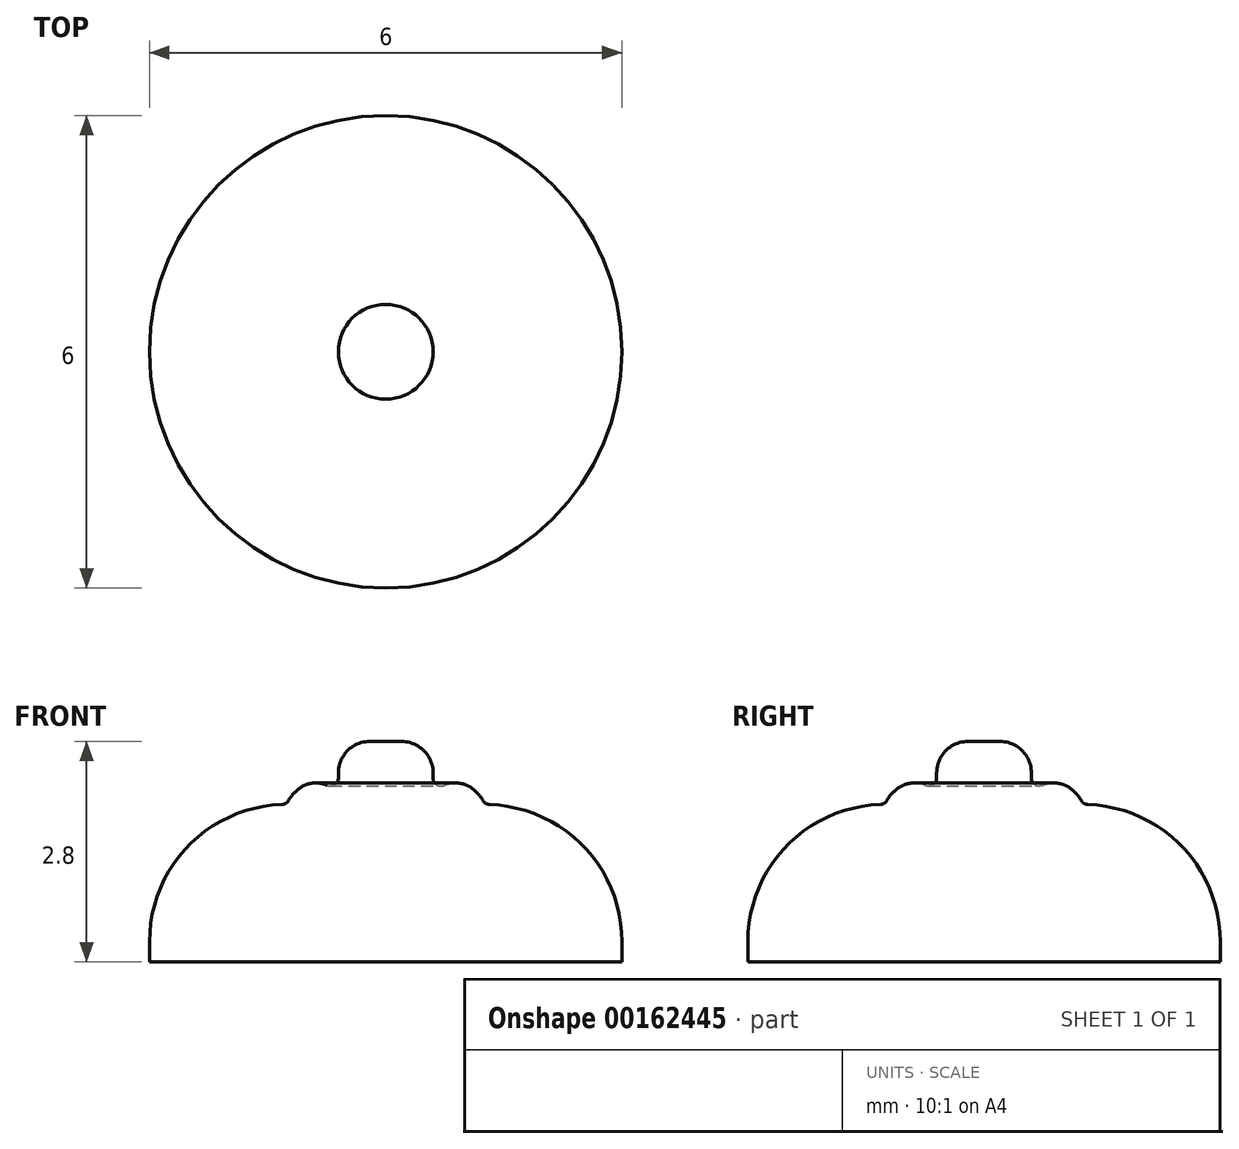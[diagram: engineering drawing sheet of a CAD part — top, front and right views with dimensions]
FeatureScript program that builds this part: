
annotation { "Feature Type Name" : "Feature", "Feature Type Description" : "" }
export const myFeature = defineFeature(function(context is Context, id is Id, definition is map)
    precondition{}
    {
        {
            var Q0;
            Q0=qCreatedBy(makeId("Top.planeOp"),FACE);
            var sketch = newSketch(context, id + "F0", { "sketchPlane" : qUnion([Q0])});
            skCircle(sketch, "E0", {"center": v(0, 0) * mm, "radius": 3 * mm});
            skSolve(sketch);
        }
        {
            var Q0;
            Q0=makeQuery(id+"F0.imprint","IMPRINT",FACE,{"disambiguationData":[TD([[makeQuery(id+"F0.imprint","IMPRINT",EDGE,{"derivedFrom":sQuery(id+"F0.wireOp",EDGE,"E0")}),1.0]])]});
            extrude(context, id + "F1", {"entities" : qUnion([Q0]), "depth" : 2 * mm});
        }
        {
            var Q0;
            Q0=makeQuery(id+"F1.opExtrude","CAP_EDGE",EDGE,{"disambiguationData":[OSD([sQuery(id+"F0.wireOp",EDGE,"E0")])],"isStart":false});
            fillet(context, id + "F2", {"entities" : qUnion([Q0]), "radius" : 1.74 * mm, "tangentPropagation" : true, "allowEdgeOverflow" : false});
        }
        {
            var Q0;
            Q0=makeQuery(id+"F1.opExtrude","CAP_FACE",FACE,{"disambiguationData":[OSD([sQuery(id+"F0.wireOp",EDGE,"E0")])],"isStart":false});
            var sketch = newSketch(context, id + "F3", { "sketchPlane" : qUnion([Q0])});
            skCircle(sketch, "E1.1", {"center": v(0, 0) * mm, "radius": 1.26 * mm});
            skSolve(sketch);
        }
        {
            var Q0;
            Q0=makeQuery(id+"F3.imprint","IMPRINT",FACE,{"disambiguationData":[TD([[makeQuery(id+"F3.imprint","IMPRINT",EDGE,{"derivedFrom":sQuery(id+"F3.wireOp",EDGE,"E1.1")}),1.0]])]});
            extrude(context, id + "F4", {"entities" : qUnion([Q0]), "operationType" : NewBodyOperationType.ADD, "depth" : .3 * mm});
        }
        {
            var Q0;
            Q0=makeQuery(id+"F4.opExtrude","CAP_EDGE",EDGE,{"disambiguationData":[OSD([sQuery(id+"F3.wireOp",EDGE,"E1.1")])],"isStart":false});
            fillet(context, id + "F5", {"entities" : qUnion([Q0]), "radius" : .5 * mm, "tangentPropagation" : true, "allowEdgeOverflow" : false});
        }
        {
            var Q0;
            Q0=makeQuery(id+"F4.opExtrude","CAP_FACE",FACE,{"disambiguationData":[OSD([sQuery(id+"F3.wireOp",EDGE,"E1.1")])],"isStart":false});
            extrude(context, id + "F6", {"entities" : qUnion([Q0]), "operationType" : NewBodyOperationType.REMOVE, "oppositeDirection" : true, "depth" : .1 * mm});
        }
        {
            var Q0;
            Q0=makeQuery(id+"F6.boolean.opBoolean","COPY",EDGE,{"derivedFrom":makeQuery(id+"F6.opExtrude","CAP_EDGE",EDGE,{"disambiguationData":[OSD([sQuery(id+"F3.wireOp",EDGE,"E1.1")])],"isStart":false})});
            fillet(context, id + "F7", {"entities" : qUnion([Q0]), "radius" : .25 * mm, "tangentPropagation" : true, "allowEdgeOverflow" : false});
        }
        {
            var Q0;
            {var subQ0=sQuery(id+"F3.wireOp",EDGE,"E1.1");Q0=makeQuery(id+"F7.opFillet","BLEND_EDGE",EDGE,{"blendedFrom":[makeQuery(id+"F6.boolean.opBoolean","COPY",EDGE,{"derivedFrom":makeQuery(id+"F6.opExtrude","CAP_EDGE",EDGE,{"disambiguationData":[OSD([subQ0])],"isStart":false})}),makeQuery(id+"F5.opFillet","BLEND_FACE",FACE,{"disambiguationData":[OSD([subQ0])]})],"blendedInto":[makeQuery(id+"F5.opFillet","BLEND_FACE",FACE,{"disambiguationData":[OSD([subQ0])]})]});}
            fillet(context, id + "F8", {"entities" : qUnion([Q0]), "radius" : .35 * mm, "tangentPropagation" : true, "allowEdgeOverflow" : false});
        }
        {
            var Q0;
            Q0=makeQuery(id+"F6.boolean.opBoolean","COPY",FACE,{"derivedFrom":makeQuery(id+"F6.opExtrude","CAP_FACE",FACE,{"disambiguationData":[OSD([sQuery(id+"F3.wireOp",EDGE,"E1.1")])],"isStart":false})});
            var sketch = newSketch(context, id + "F9", { "sketchPlane" : qUnion([Q0])});
            skCircle(sketch, "E2.0", {"center": v(0, 0) * mm, "radius": 0.6 * mm});
            skSolve(sketch);
        }
        {
            var Q0;
            Q0 = qSketchRegion(id + "F9", true);
            extrude(context, id + "F10", {"entities" : qUnion([Q0]), "operationType" : NewBodyOperationType.ADD, "depth" : .6 * mm});
        }
        {
            var Q0;
            Q0=makeQuery(id+"F10.opExtrude","CAP_EDGE",EDGE,{"disambiguationData":[OSD([sQuery(id+"F9.wireOp",EDGE,"E2.0")])],"isStart":false});
            fillet(context, id + "F11", {"entities" : qUnion([Q0]), "radius" : .4 * mm, "tangentPropagation" : true, "allowEdgeOverflow" : false});
        }
        {
            var Q0;
            {var subQ0=sQuery(id+"F3.wireOp",EDGE,"E1.1");Q0=makeQuery(id+"F10.boolean.opBoolean","MERGE",EDGE,{"derivedFrom":[makeQuery(id+"F7.opFillet","BLEND_EDGE",EDGE,{"blendedFrom":[makeQuery(id+"F6.boolean.opBoolean","COPY",EDGE,{"derivedFrom":makeQuery(id+"F6.opExtrude","CAP_EDGE",EDGE,{"disambiguationData":[OSD([subQ0])],"isStart":false})}),makeQuery(id+"F6.boolean.opBoolean","COPY",FACE,{"derivedFrom":makeQuery(id+"F6.opExtrude","CAP_FACE",FACE,{"disambiguationData":[OSD([subQ0])],"isStart":false})})],"blendedInto":[makeQuery(id+"F6.boolean.opBoolean","COPY",FACE,{"derivedFrom":makeQuery(id+"F6.opExtrude","CAP_FACE",FACE,{"disambiguationData":[OSD([subQ0])],"isStart":false})})]}),makeQuery(id+"F10.opExtrude","CAP_EDGE",EDGE,{"disambiguationData":[OSD([sQuery(id+"F9.wireOp",EDGE,"E2.0")])],"isStart":true})]});}
            fillet(context, id + "F12", {"entities" : qUnion([Q0]), "radius" : .1 * mm, "tangentPropagation" : true, "allowEdgeOverflow" : false});
        }
        {
            var Q0;
            Q0=makeQuery(id+"F5.opFillet","BLEND_EDGE",EDGE,{"blendedFrom":[makeQuery(id+"F4.opExtrude","CAP_EDGE",EDGE,{"disambiguationData":[OSD([sQuery(id+"F3.wireOp",EDGE,"E1.1")])],"isStart":false}),makeQuery(id+"F2.opFillet","BLEND_FACE",FACE,{"disambiguationData":[OSD([sQuery(id+"F0.wireOp",EDGE,"E0")])]})],"blendedInto":[makeQuery(id+"F2.opFillet","BLEND_FACE",FACE,{"disambiguationData":[OSD([sQuery(id+"F0.wireOp",EDGE,"E0")])]})]});
            fillet(context, id + "F13", {"entities" : qUnion([Q0]), "radius" : .1 * mm, "tangentPropagation" : true, "allowEdgeOverflow" : false});
        }
    });
